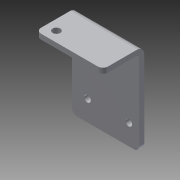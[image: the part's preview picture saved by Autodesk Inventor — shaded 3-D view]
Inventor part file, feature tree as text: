
AUTODESK INVENTOR PART (.ipt)
format: ipt  version: 2014 (Build 180170000, 170)  size: 122,880 bytes
history: native  units: in
note: dims shown in document units (in); Inventor stores cm internally (conversion verified against a paired STEP export)
features: sheet_metal_op x4, sketch x3, other x3, fillet x1
ambient origin geometry x8: Origin, YZ Plane, XZ Plane, XY Plane, X Axis, Y Axis, Z Axis, Center Point
bodies: Solid1 (feature_tree)
feature tree (11):
  sheet_metal_op  "Face1"
  sheet_metal_op  "Flange1"
  fillet  "Fillet1"  Radius=1.625in
  sketch  "Sketch1"  dims[d1=2.0in]
  other  "Plate1"
  sketch  "Sketch2"  dims[d2=0.163in]
  other  "Plate2"
  sheet_metal_op  "Bend1"
  sheet_metal_op  "Corner1"
  sketch  "Sketch4"  dims[d3=0.375in d4=0.7874in d6=1.0in d7=0.3937in d9=1.0in d11=0.125in d12=0.125in d13=0.0625in d14=0.25in d15=0.125in d16=1.0in d17=90.0deg d18=0.05in d19=0.5in d20=0.125in d21=0.125in d22=0.5in d28=0.187in d29=0.25in d31=0.125in d32=0.0in d33=0.125in d34=0.25in]
  other  "Cut2"
